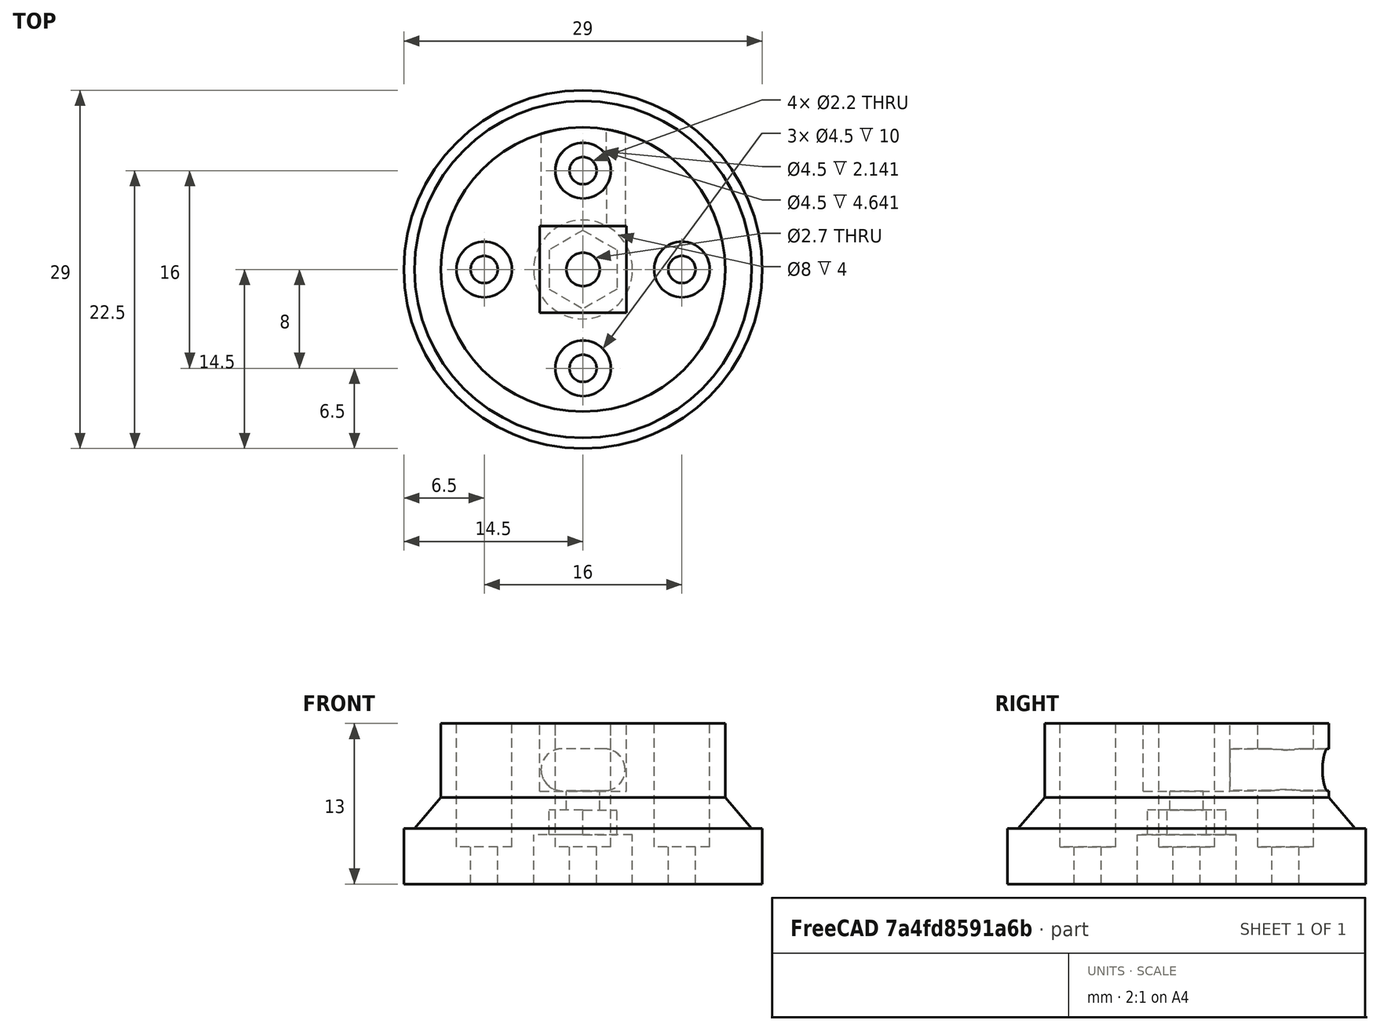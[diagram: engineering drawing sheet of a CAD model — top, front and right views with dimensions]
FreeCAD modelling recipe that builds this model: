
FCSTD DOCUMENT  (FreeCAD 0.15R4671 (Git))
Label: tendon_wheel_ax_18_3_mm
License: CC-BY 3.0
LicenseURL: http://creativecommons.org/licenses/by/3.0/
objects: Part::Cylinder×14, Part::MultiFuse×6, Part::Box×2, Part::Cone×1, Part::Extrusion×1, Part::Mirroring×1, Part::Cut×1
note: 26 computed .brp shape members not serialized (recipe doc carries the construction recipe); baked Part::Feature solids carry a one-line shape summary decoded from their .brp

FEATURE [Part::Cylinder] Cylinder
  Angle = 360
  Height = 4.5
  Placement = pos=(0,0,0.5) rot=(0,0,1;0rad)
  Radius = 14.5
FEATURE [Part::Cone] Cone
  Angle = 360
  Height = 3.5
  Placement = pos=(0,0,4) rot=(0,0,1;0rad)
  Radius1 = 14.5
  Radius2 = 11.5
FEATURE [Part::Cylinder] Cylinder001
  Angle = 360
  Height = 6.5
  Placement = pos=(0,0,7) rot=(0,0,1;0rad)
  Radius = 11.5
FEATURE [Part::Cylinder] Cylinder003  label="TopHole003"
  Angle = 360
  Height = 20
  Placement = pos=(-8,0,-3) rot=(0,0,1;0rad)
  Radius = 1.1
FEATURE [Part::Cylinder] Cylinder004  label="TopHole002"
  Angle = 360
  Height = 20
  Placement = pos=(0,-8,-3) rot=(0,0,1;0rad)
  Radius = 1.1
FEATURE [Part::Cylinder] Cylinder005  label="TopHole001"
  Angle = 360
  Height = 20
  Placement = pos=(8,0,-3) rot=(0,0,1;0rad)
  Radius = 1.1
FEATURE [Part::Cylinder] Cylinder006  label="TopHole"
  Angle = 360
  Height = 10
  Placement = pos=(0,8,-3) rot=(0,0,1;0rad)
  Radius = 1.1
FEATURE [Part::Cylinder] Cylinder007  label="TopHole004"
  Angle = 360
  Height = 20
  Placement = pos=(-8,0,3.5) rot=(0,0,1;0rad)
  Radius = 2.25
FEATURE [Part::Cylinder] Cylinder008  label="TopHole005"
  Angle = 360
  Height = 20
  Placement = pos=(8,0,3.5) rot=(0,0,1;0rad)
  Radius = 2.25
FEATURE [Part::Cylinder] Cylinder009  label="TopHole006"
  Angle = 360
  Height = 20
  Placement = pos=(0,8,3.5) rot=(0,0,1;0rad)
  Radius = 2.25
FEATURE [Part::Cylinder] Cylinder010  label="TopHole007"
  Angle = 360
  Height = 20
  Placement = pos=(0,-8,3.5) rot=(0,0,1;0rad)
  Radius = 2.25
FEATURE [Part::MultiFuse] Fusion001
  Shapes = -> [Cylinder010,Cylinder007,Cylinder005,Cylinder003,Cylinder009,Cylinder004,Cylinder008,Cylinder006]
FEATURE [Part::Cylinder] Cylinder012  label="Cylinder003"
  Angle = 360
  Height = 10
  Placement = pos=(-1.7,12,9.75) rot=(1,0,0;1.5708rad)
  Radius = 1.7
FEATURE [Part::Cylinder] Cylinder013  label="Cylinder004"
  Angle = 360
  Height = 20
  Placement = pos=(0,0,-5) rot=(0,0,1;0rad)
  Radius = 1.35
FEATURE [Part::Box] Box  label="Cube"
  Height = 8
  Length = 7
  Placement = pos=(-3.5,-3.5,8) rot=(0,0,1;0rad)
  Width = 7
FEATURE [Part::Extrusion] Extrude
  Dir = (0,0,2)
  Solid = true
FEATURE [Part::Mirroring] Part__Mirroring  label="Extrude (Mirror #1)"
  Base = (0,0,0)
  Normal = (1,0,0)
  Source = -> Extrude
FEATURE [Part::MultiFuse] Fusion002
  Placement = pos=(0,0,4.5) rot=(0,0,1;0rad)
  Shapes = -> [Part__Mirroring,Extrude]
FEATURE [Part::Cylinder] Cylinder014  label="Cylinder005"
  Angle = 360
  Height = 4.5
  Radius = 4
FEATURE [Part::Cylinder] Cylinder015  label="Cylinder006"
  Angle = 360
  Height = 10
  Placement = pos=(1.7,12,9.75) rot=(1,0,0;1.5708rad)
  Radius = 1.7
FEATURE [Part::Box] Box001  label="Cube001"
  Height = 3.4
  Length = 3.6
  Placement = pos=(-1.7,2,8.05) rot=(0,0,1;0rad)
  Width = 10
FEATURE [Part::MultiFuse] Fusion
  Shapes = -> [Cylinder,Cone,Cylinder001]
FEATURE [Part::MultiFuse] Fusion005
  Shapes = -> [Cylinder014,Fusion002,Cylinder013,Fusion001]
FEATURE [Part::MultiFuse] Fusion006
  Shapes = -> [Cylinder015,Box001,Cylinder012,Box]
FEATURE [Part::MultiFuse] Fusion007
  Shapes = -> [Fusion006,Fusion005]
FEATURE [Part::Cut] Cut
  Base = -> Fusion
  Tool = -> Fusion007
